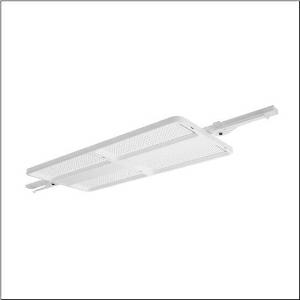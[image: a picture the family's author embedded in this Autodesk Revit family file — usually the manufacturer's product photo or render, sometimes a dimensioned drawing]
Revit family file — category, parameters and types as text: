
# Revit family: highbay_11_fur_modario_r__tragschiene_maxi_51hn12db3tma_d3d4
name_source: partatom
category: Lighting Fixtures
units: mm (PartAtom-declared; Revit-internal decimal feet)

## family parameters
Cut with Voids When Loaded = No
Host = Face
Light Source = No
Part Type = Normal
Room Calculation Point = No
Round Connector Dimension = Use Diameter
Shared = No

## types (1)
- --- (1 x LED, 53070 lm, 295.1 W, 3000K)
    Apparent Load = 295 VA
    CIE Flux Codes = 87 98 100 100 100
    Color Rendering = 80
    Color Temperature = 3000K
    Default Elevation = 1800 mm
    Description = high bay luminaire Highbay 11 for Modario® trunking rail maxi; direct symmetric wide distribution, light control with lens of PMMA; UGR ≤ 22 (X = 4H | Y = 8H | S = 0.25H | reflection values 70/50/20); luminous flux: 53.070lm; light colour: 830, colour temperature: 3000K, MacAdam ≤ 2 SDCM (initial), colour rendering: CRI > 80; luminous efficacy: 179,8lm/W; rated service life: 100.000h (L95/B50) at AT= 25°C; control: DALI 2; luminaire connection: plug, 5-pole, with phase selectionmains connection: 230..240V, AC 50/60Hz; connected load: 295,1W; protection rating (complete): IP64; insulation class (complete): insulation class I (protective earthing); protection symbol: D; impact resistance: IK07; certification: CE, ENEC, VDE, UKCA; internal wiring halogen-free; luminaire corresponds to IFS (International Featured Standards) requirements for safety and quality in the food industry; LABS conformity tested according to VDMA 24364:2018-05; housing frame of high-performance plastic PA6, matt traffic white (RAL 9016); cover of PMMA; fixing on rail side of steel, galvanised, white; blank cover of PC, traffic white (RAL 9016); dimension (LxWxH): 1.496 x 442 x 72mm; permissible operating ambient temperature: -40..+50°C (reducing of maximum allowable ambient temperature of 5°C with ceiling mounting); packaging unit: 1 piece
    Height = 72 mm  [stored 0.23622 ft]
    Lamp = 1 x LED
    Lamp Light Flux = 53070 lm
    Lamp Power = 295.1 W
    Lamp count = 1
    Length = 946 mm
    Luminous efficacy = 180 lm/W
    Manufacturer = Siteco
    ModVariant = No
    Model = 51HN12DB3TMA
    Mounting Place = Ceiling
    Mounting Type = Pendant
    Number of Poles = 1
    OnlyDefault = Yes
    Power Factor = 1
    Product Name = Highbay 11 für Modario® Tragschiene maxi
    Product group = high bay luminaire
    ProductGroupID = 901
    Protection Class = Protection class I
    Protection Degree = IP 64
    RLX_Detail_Level = 1
    RLX_Emergency_Light_Flux = 0 lm
    RLX_Emergency_Type = 0
    RLX_Emergency_Type_DB = No
    RlxData = <blob elided: 21397 chars, md5=75b71efd>
    Socket = socket
    Standby Power = 0 W
    System Light Flux = 53071 lm
    System Power = 295 W
    Type Comments = factory setting: luminous flux: 100 % | dim-lin: 254 | 664 mA
    Type Image = l_1363248.jpg
    URL = http://relux.com
    VarID = @adj_006437
    Voltage = 0 V
    Weight = 0.00 kg
    Width = 442 mm

note: [stored X ft] marks values corroborated as IEEE doubles in the binary element streams (Revit-internal decimal feet)

## geometry (parser evidence)
native form markers: Blend x4, Sweep x9
no freeform markers — native parametric forms only
